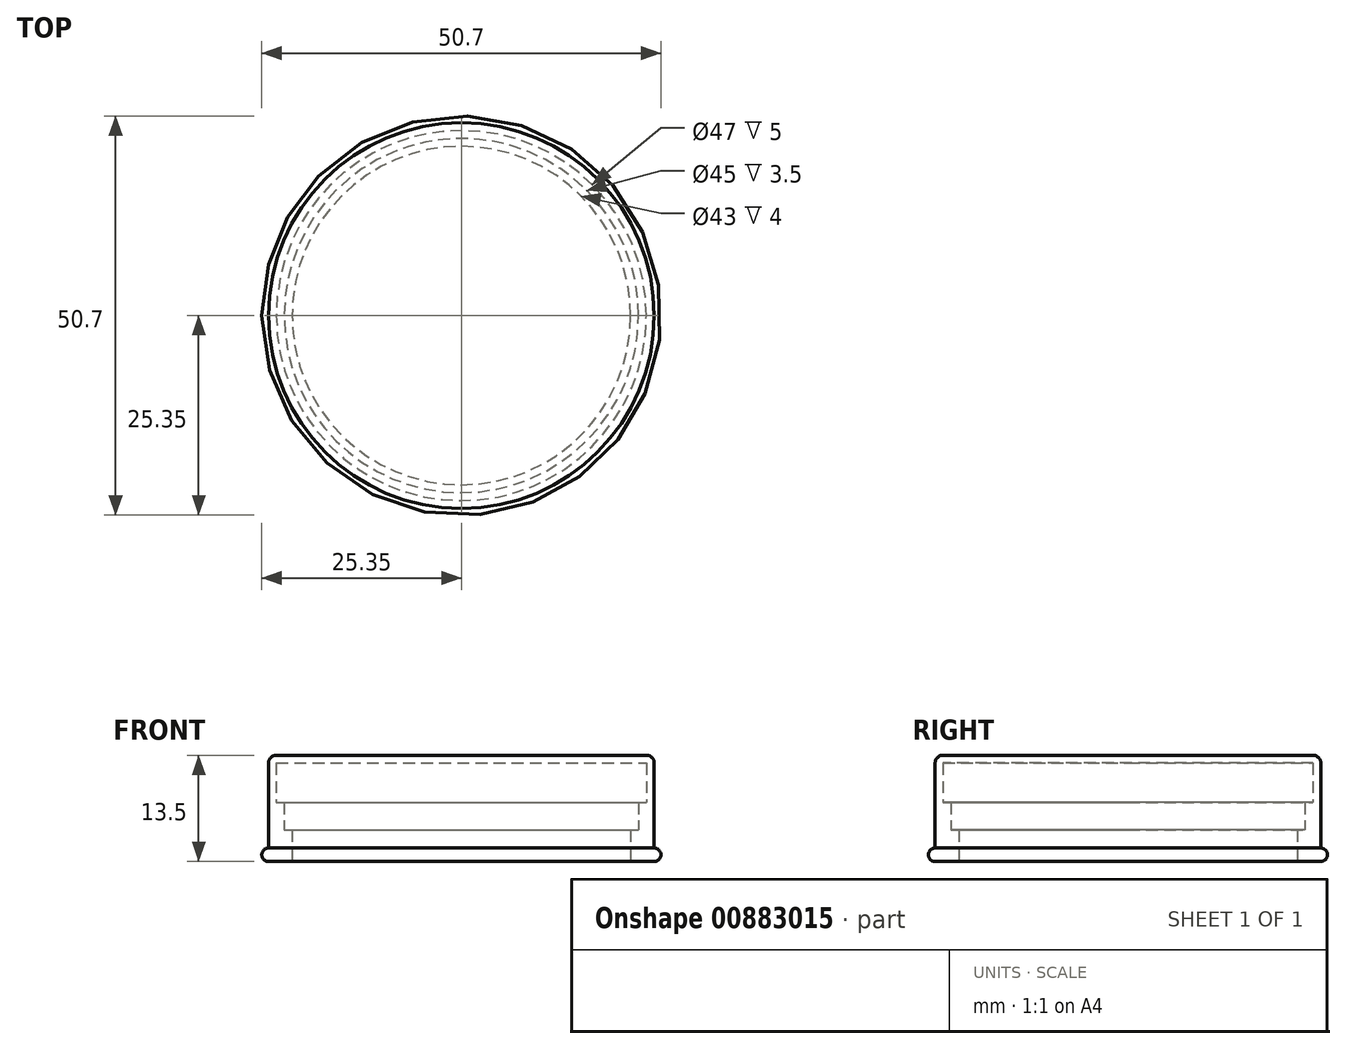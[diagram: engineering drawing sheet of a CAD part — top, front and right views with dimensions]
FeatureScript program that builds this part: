
annotation { "Feature Type Name" : "Feature", "Feature Type Description" : "" }
export const myFeature = defineFeature(function(context is Context, id is Id, definition is map)
    precondition{}
    {
        {
            var Q0;
            Q0=qCreatedBy(makeId("Right.planeOp"),FACE);
            var sketch = newSketch(context, id + "F0", { "sketchPlane" : qUnion([Q0])});
            skLineSegment(sketch, "E0", {"start": v(21.5, 0) * mm, "end": v(21.5, 4) * mm});
            skLineSegment(sketch, "E1", {"start": v(21.5, 4) * mm, "end": v(22.5, 4) * mm});
            skLineSegment(sketch, "E2", {"start": v(22.5, 4) * mm, "end": v(22.5, 7.5) * mm});
            skLineSegment(sketch, "E3", {"start": v(22.5, 7.5) * mm, "end": v(23.5, 7.5) * mm});
            skLineSegment(sketch, "E4", {"start": v(23.5, 7.5) * mm, "end": v(23.5, 12.5) * mm});
            skLineSegment(sketch, "E5", {"start": v(23.5, 12.5) * mm, "end": v(22.5, 12.5) * mm});
            skLineSegment(sketch, "E6.1", {"start": v(24.5, -0.19) * mm, "end": v(24.5, 12.5) * mm});
            skLineSegment(sketch, "E7", {"start": v(0, 0) * mm, "end": v(0, 13.5) * mm, "construction": true});
            skLineSegment(sketch, "E8", {"start": v(22.5, 12.5) * mm, "end": v(0, 12.5) * mm});
            skLineSegment(sketch, "E9", {"start": v(0, 12.5) * mm, "end": v(0, 13.5) * mm});
            skLineSegment(sketch, "E10", {"start": v(24.5, -0.19) * mm, "end": v(24.5, 0) * mm});
            skLineSegment(sketch, "E11", {"start": v(0, 13.5) * mm, "end": v(23.5, 13.5) * mm});
            skLineSegment(sketch, "E12", {"start": v(21.5, 0) * mm, "end": v(24.5, 0) * mm});
            skPoint(sketch, "E13.visualSharp", {"position": v(24.5, 13.5) * mm});
            skArc(sketch, "E13.filletArc", {"start": v(24.5, 12.5) * mm, "mid": v(24.2, 13.2) * mm, "end": v(23.5, 13.5) * mm});
            skArc(sketch, "E14", {"start": v(24.5, 0) * mm, "mid": v(25.35, 0.85) * mm, "end": v(24.5, 1.7) * mm});
            skSolve(sketch);
        }
        {
            var Q0;
            Q0=makeQuery(id+"F0.imprint","IMPRINT",FACE,{"disambiguationData":[TD([[makeQuery(id+"F0.imprint","IMPRINT",EDGE,{"derivedFrom":sQuery(id+"F0.wireOp",EDGE,"E0")}),-1.0]])]});
            var Q1;
            {var subQ0=sQuery(id+"F0.wireOp",EDGE,"gDlz97rs-IigY-FjDQ-tFoB-Qyoyegm3JKjf");Q1=makeQuery(id+"F0.imprint","IMPRINT",FACE,{"disambiguationData":[TD([[makeQuery(id+"F0.imprint","IMPRINT",EDGE,{"derivedFrom":subQ0}),1.0]])]});}
            var Q2;
            {var subQ0=sQuery(id+"F0.wireOp",EDGE,"4ImxicUg-CcNn-UCxj-KMka-mXFwro0VHIx5");Q2=makeQuery(id+"F0.imprint","IMPRINT",FACE,{"disambiguationData":[TD([[makeQuery(id+"F0.imprint","IMPRINT",EDGE,{"derivedFrom":subQ0}),1.0]])]});}
            var Q3;
            Q3=makeQuery(id+"F0.imprint","IMPRINT",FACE,{"disambiguationData":[TD([[makeQuery(id+"F0.imprint","IMPRINT",EDGE,{"derivedFrom":sQuery(id+"F0.wireOp",EDGE,"E10")}),-1.0]])]});
            var Q4;
            {var subQ0=sQuery(id+"F0.wireOp",EDGE,"E14");Q4=makeQuery(id+"F0.imprint","IMPRINT",FACE,{"disambiguationData":[TD([[makeQuery(id+"F0.imprint","IMPRINT",EDGE,{"derivedFrom":subQ0}),1.0]])]});}
            var Q5;
            Q5=sQuery(id+"F0.wireOp",EDGE,"E7");
            revolve(context, id + "F1", {"surfaceOperationType" : NewSurfaceOperationType.NEW, "entities" : qUnion([Q0, Q1, Q2, Q3, Q4]), "axis" : qUnion([Q5]), "revolveType" : RevolveType.FULL});
        }
    });
